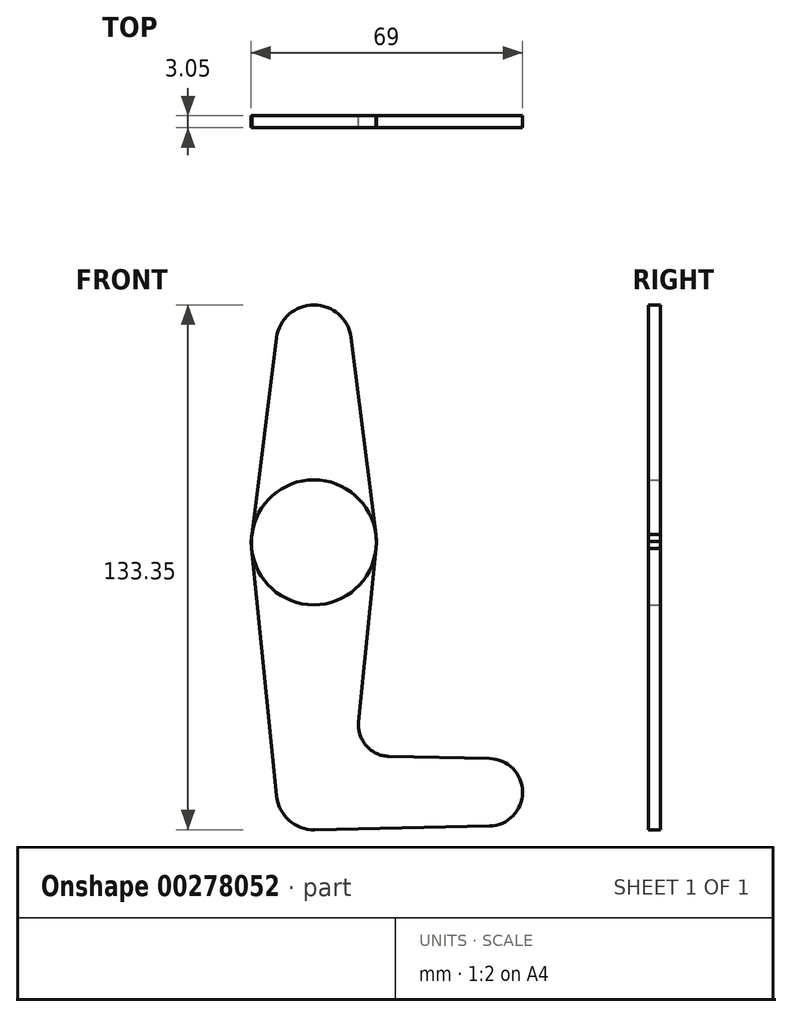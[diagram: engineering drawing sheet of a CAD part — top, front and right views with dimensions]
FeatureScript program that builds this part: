
annotation { "Feature Type Name" : "Feature", "Feature Type Description" : "" }
export const myFeature = defineFeature(function(context is Context, id is Id, definition is map)
    precondition{}
    {
        {
            var Q0;
            Q0=qCreatedBy(makeId("Front.planeOp"),FACE);
            var sketch = newSketch(context, id + "F0", { "sketchPlane" : qUnion([Q0])});
            skCircle(sketch, "E0", {"center": v(0, 0) * mm, "radius": 9.53 * mm});
            skLineSegment(sketch, "E1", {"start": v(0, 114.3) * mm, "end": v(0, 0) * mm});
            skLineSegment(sketch, "E2", {"start": v(44.45, 0) * mm, "end": v(0, 0) * mm});
            skCircle(sketch, "E3", {"center": v(0, 63.5) * mm, "radius": 15.88 * mm});
            skCircle(sketch, "E4", {"center": v(44.45, 0) * mm, "radius": 8.57 * mm});
            skCircle(sketch, "E5", {"center": v(0, 114.3) * mm, "radius": 9.53 * mm});
            skLineSegment(sketch, "E6", {"start": v(-9.45, 115.5) * mm, "end": v(-15.98, 63.7) * mm});
            skLineSegment(sketch, "E7", {"start": v(9.45, 115.5) * mm, "end": v(15.98, 63.7) * mm});
            skLineSegment(sketch, "E8", {"start": v(15.98, 63.7) * mm, "end": v(11.37, 17.86) * mm});
            skLineSegment(sketch, "E9", {"start": v(-15.98, 63.7) * mm, "end": v(-9.48, -0.95) * mm});
            skLineSegment(sketch, "E10", {"start": v(0.2, -9.52) * mm, "end": v(44.63, -8.57) * mm});
            skLineSegment(sketch, "E11", {"start": v(44.63, 8.57) * mm, "end": v(19.1, 9.12) * mm});
            skArc(sketch, "E12.filletArc", {"start": v(11.37, 17.86) * mm, "mid": v(13.33, 11.8) * mm, "end": v(19.1, 9.12) * mm});
            skSolve(sketch);
        }
        {
            var Q0;
            {var subQ0=sQuery(id+"F0.wireOp",EDGE,"E6");var subQ1=sQuery(id+"F0.wireOp",EDGE,"E3");var subQ2=makeQuery(id+"F0.imprint","INTERSECT",VERTEX,{"derivedFrom":[subQ1,subQ0]});Q0=makeQuery(id+"F0.imprint","IMPRINT",FACE,{"disambiguationData":[TD([[makeQuery(id+"F0.imprint","IMPRINT",EDGE,{"disambiguationData":[TD([[subQ2,-1.0]])],"derivedFrom":subQ1}),-1.0]])]});}
            var Q1;
            {var subQ0=sQuery(id+"F0.wireOp",EDGE,"E7");var subQ1=sQuery(id+"F0.wireOp",EDGE,"E3");var subQ2=makeQuery(id+"F0.imprint","INTERSECT",VERTEX,{"derivedFrom":[subQ1,subQ0]});Q1=makeQuery(id+"F0.imprint","IMPRINT",FACE,{"disambiguationData":[TD([[makeQuery(id+"F0.imprint","IMPRINT",EDGE,{"disambiguationData":[TD([[subQ2,1.0]])],"derivedFrom":subQ1}),-1.0]])]});}
            var Q2;
            {var subQ0=sQuery(id+"F0.wireOp",EDGE,"E4");var subQ1=makeQuery(id+"F0.imprint","INTERSECT",VERTEX,{"derivedFrom":[subQ0,sQuery(id+"F0.wireOp",EDGE,"E11")]});Q2=makeQuery(id+"F0.imprint","IMPRINT",FACE,{"disambiguationData":[TD([[makeQuery(id+"F0.imprint","IMPRINT",EDGE,{"disambiguationData":[TD([[subQ1,-1.0]])],"derivedFrom":subQ0}),1.0]])]});}
            var Q3;
            {var subQ0=sQuery(id+"F0.wireOp",EDGE,"E5");var subQ1=makeQuery(id+"F0.imprint","INTERSECT",VERTEX,{"derivedFrom":[subQ0,sQuery(id+"F0.wireOp",EDGE,"E6")]});Q3=makeQuery(id+"F0.imprint","IMPRINT",FACE,{"disambiguationData":[TD([[makeQuery(id+"F0.imprint","IMPRINT",EDGE,{"disambiguationData":[TD([[subQ1,1.0]])],"derivedFrom":subQ0}),1.0]])]});}
            var Q4;
            {var subQ0=sQuery(id+"F0.wireOp",EDGE,"E9");var subQ1=sQuery(id+"F0.wireOp",EDGE,"E0");var subQ2=makeQuery(id+"F0.imprint","INTERSECT",VERTEX,{"derivedFrom":[subQ1,subQ0]});Q4=makeQuery(id+"F0.imprint","IMPRINT",FACE,{"disambiguationData":[TD([[makeQuery(id+"F0.imprint","IMPRINT",EDGE,{"disambiguationData":[TD([[subQ2,1.0]])],"derivedFrom":subQ1}),-1.0]])]});}
            var Q5;
            {var subQ0=sQuery(id+"F0.wireOp",EDGE,"E10");Q5=makeQuery(id+"F0.imprint","IMPRINT",FACE,{"disambiguationData":[TD([[makeQuery(id+"F0.imprint","IMPRINT",EDGE,{"derivedFrom":subQ0}),1.0]])]});}
            var Q6;
            {var subQ0=sQuery(id+"F0.wireOp",EDGE,"E5");var subQ1=sQuery(id+"F0.wireOp",EDGE,"E1");var subQ2=makeQuery(id+"F0.imprint","INTERSECT",VERTEX,{"derivedFrom":[subQ1,subQ0]});Q6=makeQuery(id+"F0.imprint","IMPRINT",FACE,{"disambiguationData":[TD([[makeQuery(id+"F0.imprint","IMPRINT",EDGE,{"disambiguationData":[TD([[subQ2,-1.0]])],"derivedFrom":subQ1}),1.0]])]});}
            var Q7;
            {var subQ0=sQuery(id+"F0.wireOp",EDGE,"E5");var subQ1=sQuery(id+"F0.wireOp",EDGE,"E1");var subQ2=makeQuery(id+"F0.imprint","INTERSECT",VERTEX,{"derivedFrom":[subQ1,subQ0]});Q7=makeQuery(id+"F0.imprint","IMPRINT",FACE,{"disambiguationData":[TD([[makeQuery(id+"F0.imprint","IMPRINT",EDGE,{"disambiguationData":[TD([[subQ2,-1.0]])],"derivedFrom":subQ1}),-1.0]])]});}
            var Q8;
            {var subQ0=sQuery(id+"F0.wireOp",EDGE,"E3");var subQ1=sQuery(id+"F0.wireOp",EDGE,"E1");var subQ2=makeQuery(id+"F0.imprint","INTERSECT",VERTEX,{"disambiguationData":[OD(0.0)],"derivedFrom":[subQ1,subQ0]});Q8=makeQuery(id+"F0.imprint","IMPRINT",FACE,{"disambiguationData":[TD([[makeQuery(id+"F0.imprint","IMPRINT",EDGE,{"disambiguationData":[TD([[subQ2,-1.0]])],"derivedFrom":subQ1}),1.0]])]});}
            var Q9;
            {var subQ0=sQuery(id+"F0.wireOp",EDGE,"E3");var subQ1=sQuery(id+"F0.wireOp",EDGE,"E1");var subQ2=makeQuery(id+"F0.imprint","INTERSECT",VERTEX,{"disambiguationData":[OD(0.0)],"derivedFrom":[subQ1,subQ0]});Q9=makeQuery(id+"F0.imprint","IMPRINT",FACE,{"disambiguationData":[TD([[makeQuery(id+"F0.imprint","IMPRINT",EDGE,{"disambiguationData":[TD([[subQ2,-1.0]])],"derivedFrom":subQ1}),-1.0]])]});}
            var Q10;
            {var subQ11=sQuery(id+"F0.wireOp",EDGE,"E11");Q10=makeQuery(id+"F0.imprint","IMPRINT",FACE,{"disambiguationData":[TD([[makeQuery(id+"F0.imprint","IMPRINT",EDGE,{"derivedFrom":subQ11}),1.0]])]});}
            var Q11;
            {var subQ0=sQuery(id+"F0.wireOp",EDGE,"E0");var subQ7=makeQuery(id+"F0.imprint","INTERSECT",VERTEX,{"derivedFrom":[subQ0,sQuery(id+"F0.wireOp",EDGE,"E9")]});Q11=makeQuery(id+"F0.imprint","IMPRINT",FACE,{"disambiguationData":[TD([[makeQuery(id+"F0.imprint","IMPRINT",EDGE,{"disambiguationData":[TD([[subQ7,1.0]])],"derivedFrom":subQ0}),1.0]])]});}
            var Q12;
            {var subQ0=sQuery(id+"F0.wireOp",EDGE,"E1");var subQ1=sQuery(id+"F0.wireOp",EDGE,"E0");var subQ2=makeQuery(id+"F0.imprint","INTERSECT",VERTEX,{"derivedFrom":[subQ1,subQ0]});Q12=makeQuery(id+"F0.imprint","IMPRINT",FACE,{"disambiguationData":[TD([[makeQuery(id+"F0.imprint","IMPRINT",EDGE,{"disambiguationData":[TD([[subQ2,1.0]])],"derivedFrom":subQ1}),1.0]])]});}
            extrude(context, id + "F1", {"entities" : qUnion([Q0, Q1, Q2, Q3, Q4, Q5, Q6, Q7, Q8, Q9, Q10, Q11, Q12]), "depth" : 3.05 * mm});
        }
    });
